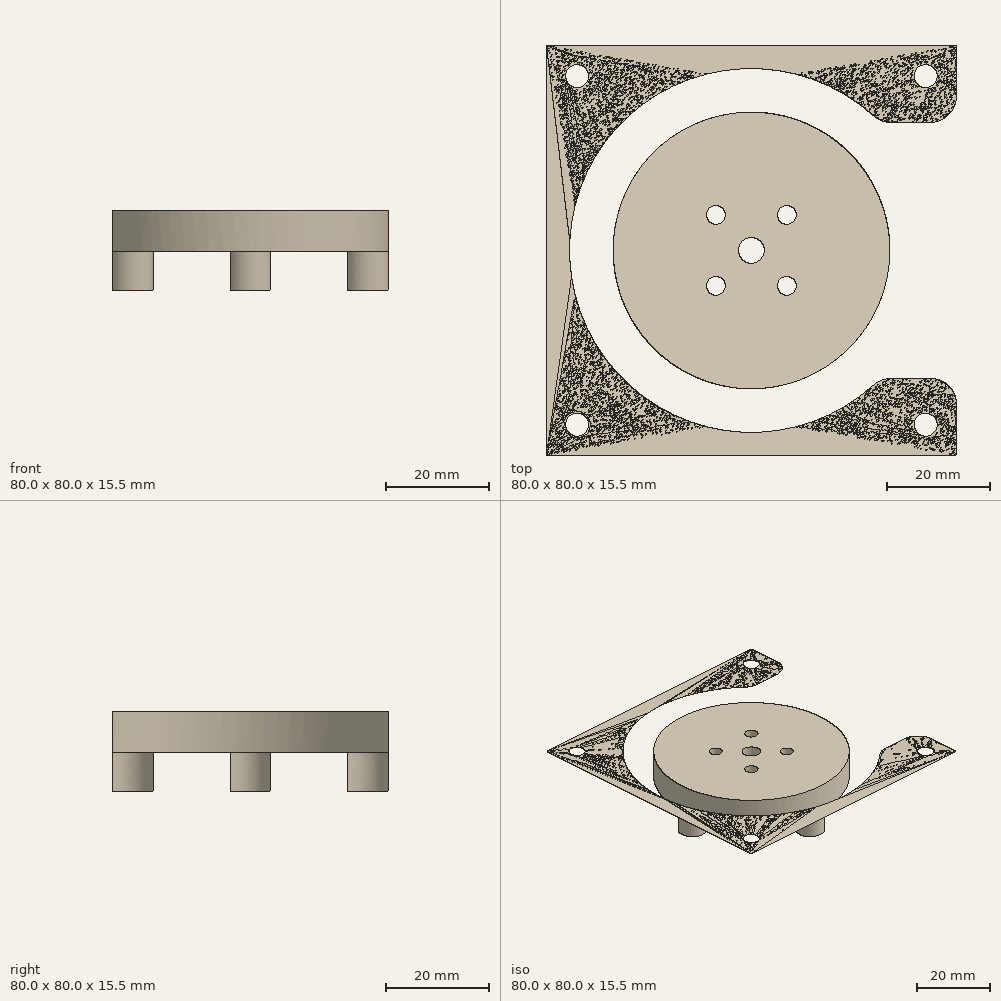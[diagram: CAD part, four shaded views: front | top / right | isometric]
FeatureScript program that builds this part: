
annotation { "Feature Type Name" : "Feature", "Feature Type Description" : "" }
export const myFeature = defineFeature(function(context is Context, id is Id, definition is map)
    precondition{}
    {
        {
            var Q0;
            Q0=qCreatedBy(makeId("Top.planeOp"),FACE);
            var sketch = newSketch(context, id + "F0", { "sketchPlane" : qUnion([Q0])});
            skLineSegment(sketch, "E0.bottom", {"start": v(40, -40) * mm, "end": v(-40, -40) * mm});
            skLineSegment(sketch, "E0.top", {"start": v(40, 40) * mm, "end": v(-40, 40) * mm});
            skLineSegment(sketch, "E0.left", {"start": v(40, -40) * mm, "end": v(40, -10) * mm});
            skLineSegment(sketch, "E0.right", {"start": v(-40, -40) * mm, "end": v(-40, 40) * mm});
            skPoint(sketch, "E0.middle", {"position": v(0, 0) * mm});
            skLineSegment(sketch, "E1.bottom", {"start": v(-15.5, 15.5) * mm, "end": v(15.5, 15.5) * mm, "construction": true});
            skLineSegment(sketch, "E1.top", {"start": v(-15.5, -15.5) * mm, "end": v(15.5, -15.5) * mm, "construction": true});
            skLineSegment(sketch, "E1.left", {"start": v(-15.5, 15.5) * mm, "end": v(-15.5, -15.5) * mm, "construction": true});
            skLineSegment(sketch, "E1.right", {"start": v(15.5, 15.5) * mm, "end": v(15.5, -15.5) * mm, "construction": true});
            skCircle(sketch, "E2", {"center": v(-15.5, 15.5) * mm, "radius": 1.75 * mm});
            skCircle(sketch, "E3", {"center": v(15.5, 15.5) * mm, "radius": 1.75 * mm});
            skCircle(sketch, "E4", {"center": v(15.5, -15.5) * mm, "radius": 1.75 * mm});
            skCircle(sketch, "E5", {"center": v(-15.5, -15.5) * mm, "radius": 1.75 * mm});
            skArc(sketch, "E6", {"start": v(16.2, 7.83) * mm, "mid": v(-18, 0) * mm, "end": v(16.2, -7.83) * mm});
            skLineSegment(sketch, "E7.0", {"start": v(34, 34) * mm, "end": v(-34, 34) * mm, "construction": true});
            skLineSegment(sketch, "E7.1", {"start": v(34, -34) * mm, "end": v(34, 34) * mm, "construction": true});
            skLineSegment(sketch, "E7.2", {"start": v(34, -34) * mm, "end": v(-34, -34) * mm, "construction": true});
            skLineSegment(sketch, "E7.3", {"start": v(-34, -34) * mm, "end": v(-34, 34) * mm, "construction": true});
            skCircle(sketch, "E8", {"center": v(-34, 34) * mm, "radius": 2.25 * mm});
            skCircle(sketch, "E9", {"center": v(34, 34) * mm, "radius": 2.25 * mm});
            skCircle(sketch, "E10", {"center": v(34, -34) * mm, "radius": 2.25 * mm});
            skCircle(sketch, "E11", {"center": v(-34, -34) * mm, "radius": 2.25 * mm});
            skCircle(sketch, "E12", {"center": v(-15.5, 15.5) * mm, "radius": 3 * mm});
            skCircle(sketch, "E13", {"center": v(15.5, 15.5) * mm, "radius": 3 * mm});
            skCircle(sketch, "E14", {"center": v(15.5, -15.5) * mm, "radius": 3 * mm});
            skCircle(sketch, "E15", {"center": v(-15.5, -15.5) * mm, "radius": 3 * mm});
            skLineSegment(sketch, "E16", {"start": v(20.71, 5) * mm, "end": v(35, 5) * mm});
            skLineSegment(sketch, "E17", {"start": v(20.71, -5) * mm, "end": v(35, -5) * mm});
            skLineSegment(sketch, "E18.trimOffspring", {"start": v(40, 10) * mm, "end": v(40, 40) * mm});
            skPoint(sketch, "E19.orphan", {"position": v(18, 0) * mm});
            skPoint(sketch, "E20.end.orphan", {"position": v(40, 0) * mm});
            skPoint(sketch, "E21.visualSharp", {"position": v(17.3, 5) * mm});
            skArc(sketch, "E21.filletArc", {"start": v(16.2, 7.83) * mm, "mid": v(18.05, 5.77) * mm, "end": v(20.71, 5) * mm});
            skPoint(sketch, "E22.visualSharp", {"position": v(17.3, -5) * mm});
            skArc(sketch, "E22.filletArc", {"start": v(20.71, -5) * mm, "mid": v(18.05, -5.77) * mm, "end": v(16.2, -7.83) * mm});
            skPoint(sketch, "E23.visualSharp", {"position": v(40, -5) * mm});
            skArc(sketch, "E23.filletArc", {"start": v(40, -10) * mm, "mid": v(38.54, -6.46) * mm, "end": v(35, -5) * mm});
            skPoint(sketch, "E24.visualSharp", {"position": v(40, 5) * mm});
            skArc(sketch, "E24.filletArc", {"start": v(35, 5) * mm, "mid": v(38.54, 6.46) * mm, "end": v(40, 10) * mm});
            skSolve(sketch);
        }
        {
            var Q0;
            Q0=makeQuery(id+"F0.imprint","IMPRINT",FACE,{"disambiguationData":[TD([[makeQuery(id+"F0.imprint","IMPRINT",EDGE,{"derivedFrom":sQuery(id+"F0.wireOp",EDGE,"E2")}),-1.0]])]});
            var Q1;
            Q1=makeQuery(id+"F0.imprint","IMPRINT",FACE,{"disambiguationData":[TD([[makeQuery(id+"F0.imprint","IMPRINT",EDGE,{"derivedFrom":sQuery(id+"F0.wireOp",EDGE,"E5")}),-1.0]])]});
            var Q2;
            Q2=makeQuery(id+"F0.imprint","IMPRINT",FACE,{"disambiguationData":[TD([[makeQuery(id+"F0.imprint","IMPRINT",EDGE,{"derivedFrom":sQuery(id+"F0.wireOp",EDGE,"E4")}),-1.0]])]});
            var Q3;
            Q3=makeQuery(id+"F0.imprint","IMPRINT",FACE,{"disambiguationData":[TD([[makeQuery(id+"F0.imprint","IMPRINT",EDGE,{"derivedFrom":sQuery(id+"F0.wireOp",EDGE,"E3")}),-1.0]])]});
            var Q4;
            Q4=makeQuery(id+"F0.imprint","IMPRINT",FACE,{"disambiguationData":[TD([[makeQuery(id+"F0.imprint","IMPRINT",EDGE,{"derivedFrom":sQuery(id+"F0.wireOp",EDGE,"E0.bottom")}),-1.0]])]});
            extrude(context, id + "F1", {"entities" : qUnion([Q0, Q1, Q2, Q3, Q4]), "depth" : 1 / 50.8 * mm});
        }
        {
            var Q0;
            Q0=makeQuery(id+"F1.opExtrude","CAP_FACE",FACE,{"disambiguationData":[OSD([sQuery(id+"F0.wireOp",EDGE,"E0.bottom"),sQuery(id+"F0.wireOp",EDGE,"E0.top"),sQuery(id+"F0.wireOp",EDGE,"E0.left"),sQuery(id+"F0.wireOp",EDGE,"E0.right"),sQuery(id+"F0.wireOp",EDGE,"E2"),sQuery(id+"F0.wireOp",EDGE,"E3"),sQuery(id+"F0.wireOp",EDGE,"E4"),sQuery(id+"F0.wireOp",EDGE,"E5"),sQuery(id+"F0.wireOp",EDGE,"E6"),sQuery(id+"F0.wireOp",EDGE,"E8"),sQuery(id+"F0.wireOp",EDGE,"E9"),sQuery(id+"F0.wireOp",EDGE,"E10"),sQuery(id+"F0.wireOp",EDGE,"E11"),sQuery(id+"F0.wireOp",EDGE,"E16"),sQuery(id+"F0.wireOp",EDGE,"E17"),sQuery(id+"F0.wireOp",EDGE,"E18.trimOffspring"),sQuery(id+"F0.wireOp",EDGE,"E21.filletArc"),sQuery(id+"F0.wireOp",EDGE,"E22.filletArc"),sQuery(id+"F0.wireOp",EDGE,"E23.filletArc"),sQuery(id+"F0.wireOp",EDGE,"E24.filletArc")])],"isStart":false});
            var sketch = newSketch(context, id + "F2", { "sketchPlane" : qUnion([Q0])});
            skCircle(sketch, "E25", {"center": v(-15.5, 15.5) * mm, "radius": 3 * mm});
            skCircle(sketch, "E26", {"center": v(15.5, 15.5) * mm, "radius": 3 * mm});
            skCircle(sketch, "E27", {"center": v(15.5, -15.5) * mm, "radius": 3 * mm});
            skCircle(sketch, "E28", {"center": v(-15.5, -15.5) * mm, "radius": 3 * mm});
            skSolve(sketch);
        }
        {
            var Q0;
            Q0 = qSketchRegion(id + "F2", true);
            extrude(context, id + "F3", {"entities" : qUnion([Q0]), "operationType" : NewBodyOperationType.REMOVE, "oppositeDirection" : true, "depth" : 3 * mm});
        }
        {
            var Q0;
            Q0=qCreatedBy(makeId("Top.planeOp"),FACE);
            var sketch = newSketch(context, id + "F4", { "sketchPlane" : qUnion([Q0])});
            skCircle(sketch, "E29", {"center": v(-34, 34) * mm, "radius": 2.55 * mm});
            skCircle(sketch, "E30", {"center": v(34, 34) * mm, "radius": 2.55 * mm});
            skCircle(sketch, "E31", {"center": v(34, -34) * mm, "radius": 2.55 * mm});
            skCircle(sketch, "E32", {"center": v(-34, -34) * mm, "radius": 2.55 * mm});
            skCircle(sketch, "E33.converted", {"center": v(0, 0) * mm, "radius": 27.5 * mm});
            skLineSegment(sketch, "E34.bottom", {"start": v(-40, 40) * mm, "end": v(40, 40) * mm});
            skLineSegment(sketch, "E34.top", {"start": v(-40, -40) * mm, "end": v(40, -40) * mm});
            skLineSegment(sketch, "E34.left", {"start": v(-40, 40) * mm, "end": v(-40, -40) * mm});
            skLineSegment(sketch, "E35", {"start": v(40, 40) * mm, "end": v(55, 40) * mm});
            skLineSegment(sketch, "E36", {"start": v(55, 40) * mm, "end": v(55, -40) * mm});
            skLineSegment(sketch, "E37", {"start": v(55, -40) * mm, "end": v(40, -40) * mm});
            skSolve(sketch);
        }
        {
            var Q0;
            Q0=makeQuery(id+"F4.imprint","IMPRINT",FACE,{"disambiguationData":[TD([[makeQuery(id+"F4.imprint","IMPRINT",EDGE,{"derivedFrom":sQuery(id+"F4.wireOp",EDGE,"SzwYI1oz-XZVD-BAMc-ip5V-dh6fbSi5rG3T.left")}),1.0]])]});
            var Q1;
            Q1=makeQuery(id+"F4.imprint","IMPRINT",FACE,{"disambiguationData":[TD([[makeQuery(id+"F4.imprint","IMPRINT",EDGE,{"derivedFrom":sQuery(id+"F4.wireOp",EDGE,"E29")}),-1.0]])]});
            extrude(context, id + "F5", {"entities" : qUnion([Q0, Q1]), "depth" : 1 / 50.8 * mm});
        }
        {
            var Q0;
            Q0=makeQuery(id+"F5.opExtrude","CAP_FACE",FACE,{"disambiguationData":[OSD([sQuery(id+"F4.wireOp",EDGE,"E29"),sQuery(id+"F4.wireOp",EDGE,"E30"),sQuery(id+"F4.wireOp",EDGE,"E31"),sQuery(id+"F4.wireOp",EDGE,"E32"),sQuery(id+"F4.wireOp",EDGE,"E33.converted"),sQuery(id+"F4.wireOp",EDGE,"E34.bottom"),sQuery(id+"F4.wireOp",EDGE,"E34.top"),sQuery(id+"F4.wireOp",EDGE,"E34.left"),sQuery(id+"F4.wireOp",EDGE,"E35"),sQuery(id+"F4.wireOp",EDGE,"E36"),sQuery(id+"F4.wireOp",EDGE,"E37")])],"isStart":false});
            var sketch = newSketch(context, id + "F6", { "sketchPlane" : qUnion([Q0])});
            skLineSegment(sketch, "E38", {"start": v(0, 0) * mm, "end": v(55, 0) * mm, "construction": true});
            skArc(sketch, "E39", {"start": v(23.85, 26.3) * mm, "mid": v(-35.5, 0) * mm, "end": v(23.85, -26.3) * mm});
            skLineSegment(sketch, "E40", {"start": v(27.2, 25) * mm, "end": v(35, 25) * mm});
            skLineSegment(sketch, "E41", {"start": v(27.2, -25) * mm, "end": v(35, -25) * mm});
            skLineSegment(sketch, "E42", {"start": v(55, 40) * mm, "end": v(55, -40) * mm});
            skLineSegment(sketch, "E43", {"start": v(55, -40) * mm, "end": v(40, -40) * mm});
            skLineSegment(sketch, "E44", {"start": v(55, 40) * mm, "end": v(40, 40) * mm});
            skLineSegment(sketch, "E45", {"start": v(40, 40) * mm, "end": v(40, 30) * mm});
            skLineSegment(sketch, "E46", {"start": v(40, -40) * mm, "end": v(40, -30) * mm});
            skPoint(sketch, "E47.orphan", {"position": v(55, 25) * mm});
            skPoint(sketch, "E48.orphan", {"position": v(55, -25) * mm});
            skPoint(sketch, "E49.visualSharp", {"position": v(25.2, 25) * mm});
            skArc(sketch, "E49.filletArc", {"start": v(23.85, 26.3) * mm, "mid": v(25.4, 25.34) * mm, "end": v(27.2, 25) * mm});
            skPoint(sketch, "E50.visualSharp", {"position": v(25.2, -25) * mm});
            skArc(sketch, "E50.filletArc", {"start": v(27.2, -25) * mm, "mid": v(25.4, -25.34) * mm, "end": v(23.85, -26.3) * mm});
            skPoint(sketch, "E51.visualSharp", {"position": v(40, 25) * mm});
            skArc(sketch, "E51.filletArc", {"start": v(35, 25) * mm, "mid": v(38.54, 26.46) * mm, "end": v(40, 30) * mm});
            skPoint(sketch, "E52.visualSharp", {"position": v(40, -25) * mm});
            skArc(sketch, "E52.filletArc", {"start": v(40, -30) * mm, "mid": v(38.54, -26.46) * mm, "end": v(35, -25) * mm});
            skSolve(sketch);
        }
        {
            var Q0;
            Q0 = qSketchRegion(id + "F6", true);
            extrude(context, id + "F7", {"entities" : qUnion([Q0]), "operationType" : NewBodyOperationType.REMOVE, "oppositeDirection" : true, "depth" : 7.5 * mm});
        }
        {
            var Q0;
            Q0=makeQuery(id+"F1.opExtrude","CAP_FACE",FACE,{"disambiguationData":[OSD([sQuery(id+"F0.wireOp",EDGE,"E0.bottom"),sQuery(id+"F0.wireOp",EDGE,"E0.top"),sQuery(id+"F0.wireOp",EDGE,"E0.left"),sQuery(id+"F0.wireOp",EDGE,"E0.right"),sQuery(id+"F0.wireOp",EDGE,"E2"),sQuery(id+"F0.wireOp",EDGE,"E3"),sQuery(id+"F0.wireOp",EDGE,"E4"),sQuery(id+"F0.wireOp",EDGE,"E5"),sQuery(id+"F0.wireOp",EDGE,"E6"),sQuery(id+"F0.wireOp",EDGE,"E8"),sQuery(id+"F0.wireOp",EDGE,"E9"),sQuery(id+"F0.wireOp",EDGE,"E10"),sQuery(id+"F0.wireOp",EDGE,"E11")])],"isStart":false});
            var sketch = newSketch(context, id + "F8", { "sketchPlane" : qUnion([Q0])});
            skCircle(sketch, "E53", {"center": v(0, 0) * mm, "radius": 27 * mm});
            skCircle(sketch, "E54", {"center": v(0, 0) * mm, "radius": 2.5 * mm});
            skCircle(sketch, "E55", {"center": v(0, 0) * mm, "radius": 9.78 * mm, "construction": true});
            skLineSegment(sketch, "E56", {"start": v(-6.91, 6.91) * mm, "end": v(6.91, -6.91) * mm, "construction": true});
            skLineSegment(sketch, "E57", {"start": v(0, 0) * mm, "end": v(9.78, 0) * mm, "construction": true});
            skLineSegment(sketch, "E58", {"start": v(6.91, 6.91) * mm, "end": v(-6.91, -6.91) * mm, "construction": true});
            skCircle(sketch, "E59", {"center": v(-6.91, 6.91) * mm, "radius": 1.83 * mm});
            skCircle(sketch, "E60", {"center": v(6.91, 6.91) * mm, "radius": 1.83 * mm});
            skCircle(sketch, "E61", {"center": v(-6.91, -6.91) * mm, "radius": 1.83 * mm});
            skCircle(sketch, "E62", {"center": v(6.91, -6.91) * mm, "radius": 1.83 * mm});
            skSolve(sketch);
        }
        {
            var Q0;
            Q0=makeQuery(id+"F8.imprint","IMPRINT",FACE,{"disambiguationData":[TD([[makeQuery(id+"F8.imprint","IMPRINT",EDGE,{"derivedFrom":sQuery(id+"F8.wireOp",EDGE,"E54")}),-1.0]])]});
            var Q1;
            Q1=makeQuery(id+"F8.imprint","IMPRINT",FACE,{"disambiguationData":[TD([[makeQuery(id+"F8.imprint","IMPRINT",EDGE,{"derivedFrom":sQuery(id+"F8.wireOp",EDGE,"E53")}),1.0]])]});
            var Q2;
            Q2=makeQuery(id+"F8.imprint","IMPRINT",FACE,{"disambiguationData":[TD([[makeQuery(id+"F8.imprint","IMPRINT",EDGE,{"derivedFrom":makeQuery(id+"FTrI075hzfV4mjk_1.boolean.opBoolean","COPY",EDGE,{"derivedFrom":makeQuery(id+"FTrI075hzfV4mjk_1.opExtrude","CAP_EDGE",EDGE,{"disambiguationData":[OSD([sQuery(id+"FShpH3dh1RRvTy6_1.wireOp",EDGE,"Xwm17QTd-3DcS-amAB-pC5Q-tTTMqDfQ7fXi")])],"isStart":true})})}),1.0]])]});
            var Q3;
            Q3=makeQuery(id+"F8.imprint","IMPRINT",FACE,{"disambiguationData":[TD([[makeQuery(id+"F8.imprint","IMPRINT",EDGE,{"derivedFrom":makeQuery(id+"FTrI075hzfV4mjk_1.boolean.opBoolean","COPY",EDGE,{"derivedFrom":makeQuery(id+"FTrI075hzfV4mjk_1.opExtrude","CAP_EDGE",EDGE,{"disambiguationData":[OSD([sQuery(id+"FShpH3dh1RRvTy6_1.wireOp",EDGE,"d2arbUhB-REkU-1kOk-skPT-kg5tykuWPc0J")])],"isStart":true})})}),1.0]])]});
            var Q4;
            Q4=makeQuery(id+"F8.imprint","IMPRINT",FACE,{"disambiguationData":[TD([[makeQuery(id+"F8.imprint","IMPRINT",EDGE,{"derivedFrom":makeQuery(id+"FTrI075hzfV4mjk_1.boolean.opBoolean","COPY",EDGE,{"derivedFrom":makeQuery(id+"FTrI075hzfV4mjk_1.opExtrude","CAP_EDGE",EDGE,{"disambiguationData":[OSD([sQuery(id+"FShpH3dh1RRvTy6_1.wireOp",EDGE,"5IFNQj8m-EtSP-AZDj-6iIX-tpVIsCcxwfQm")])],"isStart":true})})}),1.0]])]});
            var Q5;
            Q5=makeQuery(id+"F8.imprint","IMPRINT",FACE,{"disambiguationData":[TD([[makeQuery(id+"F8.imprint","IMPRINT",EDGE,{"derivedFrom":makeQuery(id+"FTrI075hzfV4mjk_1.boolean.opBoolean","COPY",EDGE,{"derivedFrom":makeQuery(id+"FTrI075hzfV4mjk_1.opExtrude","CAP_EDGE",EDGE,{"disambiguationData":[OSD([sQuery(id+"FShpH3dh1RRvTy6_1.wireOp",EDGE,"SwQGWjXq-FfIZ-T29M-yHBs-btcCn4ratvJy")])],"isStart":true})})}),1.0]])]});
            extrude(context, id + "F9", {"entities" : qUnion([Q0, Q1, Q2, Q3, Q4, Q5]), "depth" : 1 / 50.8 * mm - 8 * mm});
        }
        {
            var Q0;
            Q0=makeQuery(id+"F9.opExtrude","CAP_FACE",FACE,{"disambiguationData":[OSD([sQuery(id+"F8.wireOp",EDGE,"E53"),sQuery(id+"F8.wireOp",EDGE,"E54"),sQuery(id+"F8.wireOp",EDGE,"UeMavwyI-2tpu-FiCq-koQm-kxTMfEQhDMBH"),sQuery(id+"F8.wireOp",EDGE,"3WjjRdRL-Riah-sT7i-ymha-JiXvzbBVFymv"),sQuery(id+"F8.wireOp",EDGE,"8zFeG0Rn-Ynww-ORRa-GC0K-8XyZDYeYF68g"),sQuery(id+"F8.wireOp",EDGE,"nbaDkFKX-ZnkR-jH7f-ZXnJ-WNvkg8F9Y6cW")])],"isStart":false});
            var sketch = newSketch(context, id + "F10", { "sketchPlane" : qUnion([Q0])});
            skCircle(sketch, "E63", {"center": v(0, 0) * mm, "radius": 27 * mm});
            skCircle(sketch, "E64.0", {"center": v(0, 0) * mm, "radius": 23 * mm, "construction": true});
            skCircle(sketch, "E65", {"center": v(0, 23) * mm, "radius": 4 * mm});
            skCircle(sketch, "E66", {"center": v(-23, 0) * mm, "radius": 4 * mm});
            skCircle(sketch, "E67", {"center": v(0, -23) * mm, "radius": 4 * mm});
            skCircle(sketch, "E68", {"center": v(23, 0) * mm, "radius": 4 * mm});
            skSolve(sketch);
        }
        {
            var Q0;
            Q0=makeQuery(id+"F10.imprint","IMPRINT",FACE,{"disambiguationData":[TD([[makeQuery(id+"F10.imprint","IMPRINT",EDGE,{"derivedFrom":sQuery(id+"F10.wireOp",EDGE,"E65")}),1.0]])]});
            var Q1;
            Q1=makeQuery(id+"F10.imprint","IMPRINT",FACE,{"disambiguationData":[TD([[makeQuery(id+"F10.imprint","IMPRINT",EDGE,{"derivedFrom":sQuery(id+"F10.wireOp",EDGE,"E66")}),1.0]])]});
            var Q2;
            Q2=makeQuery(id+"F10.imprint","IMPRINT",FACE,{"disambiguationData":[TD([[makeQuery(id+"F10.imprint","IMPRINT",EDGE,{"derivedFrom":sQuery(id+"F10.wireOp",EDGE,"E67")}),1.0]])]});
            var Q3;
            Q3=makeQuery(id+"F10.imprint","IMPRINT",FACE,{"disambiguationData":[TD([[makeQuery(id+"F10.imprint","IMPRINT",EDGE,{"derivedFrom":sQuery(id+"F10.wireOp",EDGE,"E68")}),1.0]])]});
            var Q4;
            Q4=sQuery(id+"F10.wireOp",EDGE,"E66");
            var Q5;
            Q5=sQuery(id+"F10.wireOp",EDGE,"E65");
            var Q6;
            Q6=sQuery(id+"F10.wireOp",EDGE,"E68");
            var Q7;
            Q7=sQuery(id+"F10.wireOp",EDGE,"E67");
            extrude(context, id + "F11", {"entities" : qUnion([Q0, Q1, Q2, Q3]), "operationType" : NewBodyOperationType.ADD, "surfaceEntities" : qUnion([Q4, Q5, Q6, Q7]), "depth" : 7.5 * mm});
        }
        {
            var Q0;
            Q0=makeQuery(id+"F9.opExtrude","CAP_FACE",FACE,{"disambiguationData":[OSD([sQuery(id+"F8.wireOp",EDGE,"E53"),sQuery(id+"F8.wireOp",EDGE,"E54"),sQuery(id+"F8.wireOp",EDGE,"UeMavwyI-2tpu-FiCq-koQm-kxTMfEQhDMBH"),sQuery(id+"F8.wireOp",EDGE,"3WjjRdRL-Riah-sT7i-ymha-JiXvzbBVFymv"),sQuery(id+"F8.wireOp",EDGE,"8zFeG0Rn-Ynww-ORRa-GC0K-8XyZDYeYF68g"),sQuery(id+"F8.wireOp",EDGE,"nbaDkFKX-ZnkR-jH7f-ZXnJ-WNvkg8F9Y6cW")])],"isStart":false});
            var sketch = newSketch(context, id + "F12", { "sketchPlane" : qUnion([Q0])});
            skCircle(sketch, "E69", {"center": v(-6.91, -6.91) * mm, "radius": 3.56 * mm});
            skCircle(sketch, "E70", {"center": v(-6.91, 6.91) * mm, "radius": 3.56 * mm});
            skCircle(sketch, "E71", {"center": v(6.91, 6.91) * mm, "radius": 3.56 * mm});
            skCircle(sketch, "E72", {"center": v(6.91, -6.91) * mm, "radius": 3.56 * mm});
            skSolve(sketch);
        }
        {
            var Q0;
            Q0=makeQuery(id+"F12.imprint","IMPRINT",FACE,{"disambiguationData":[TD([[makeQuery(id+"F12.imprint","IMPRINT",EDGE,{"derivedFrom":sQuery(id+"F12.wireOp",EDGE,"cc31BglZ-yt0O-0zj4-zDYO-pge4Y2LM6wMn")}),1.0]])]});
            var Q1;
            Q1=makeQuery(id+"F12.imprint","IMPRINT",FACE,{"disambiguationData":[TD([[makeQuery(id+"F12.imprint","IMPRINT",EDGE,{"derivedFrom":sQuery(id+"F12.wireOp",EDGE,"dkaVZ7zl-2tHi-M4wM-Z75O-2oqmA8DrdUIm")}),1.0]])]});
            var Q2;
            Q2=makeQuery(id+"F12.imprint","IMPRINT",FACE,{"disambiguationData":[TD([[makeQuery(id+"F12.imprint","IMPRINT",EDGE,{"derivedFrom":sQuery(id+"F12.wireOp",EDGE,"HLHbHlMh-fpWh-sNk5-FQOY-WqZQPMSyyd9O")}),1.0]])]});
            var Q3;
            Q3=makeQuery(id+"F12.imprint","IMPRINT",FACE,{"disambiguationData":[TD([[makeQuery(id+"F12.imprint","IMPRINT",EDGE,{"derivedFrom":sQuery(id+"F12.wireOp",EDGE,"631SNhfv-Kbc1-GVY8-q3pN-X1cctjdwrfRc")}),1.0]])]});
            var Q4;
            Q4=makeQuery(id+"F12.imprint","IMPRINT",FACE,{"disambiguationData":[TD([[makeQuery(id+"F12.imprint","IMPRINT",EDGE,{"derivedFrom":sQuery(id+"F12.wireOp",EDGE,"E69")}),1.0]])]});
            var Q5;
            Q5=makeQuery(id+"F12.imprint","IMPRINT",FACE,{"disambiguationData":[TD([[makeQuery(id+"F12.imprint","IMPRINT",EDGE,{"derivedFrom":sQuery(id+"F12.wireOp",EDGE,"E70")}),1.0]])]});
            var Q6;
            Q6=makeQuery(id+"F12.imprint","IMPRINT",FACE,{"disambiguationData":[TD([[makeQuery(id+"F12.imprint","IMPRINT",EDGE,{"derivedFrom":sQuery(id+"F12.wireOp",EDGE,"E71")}),1.0]])]});
            var Q7;
            Q7=makeQuery(id+"F12.imprint","IMPRINT",FACE,{"disambiguationData":[TD([[makeQuery(id+"F12.imprint","IMPRINT",EDGE,{"derivedFrom":sQuery(id+"F12.wireOp",EDGE,"E72")}),1.0]])]});
            extrude(context, id + "F13", {"entities" : qUnion([Q0, Q1, Q2, Q3, Q4, Q5, Q6, Q7]), "operationType" : NewBodyOperationType.REMOVE, "oppositeDirection" : true, "depth" : 3 * mm});
        }
    });
